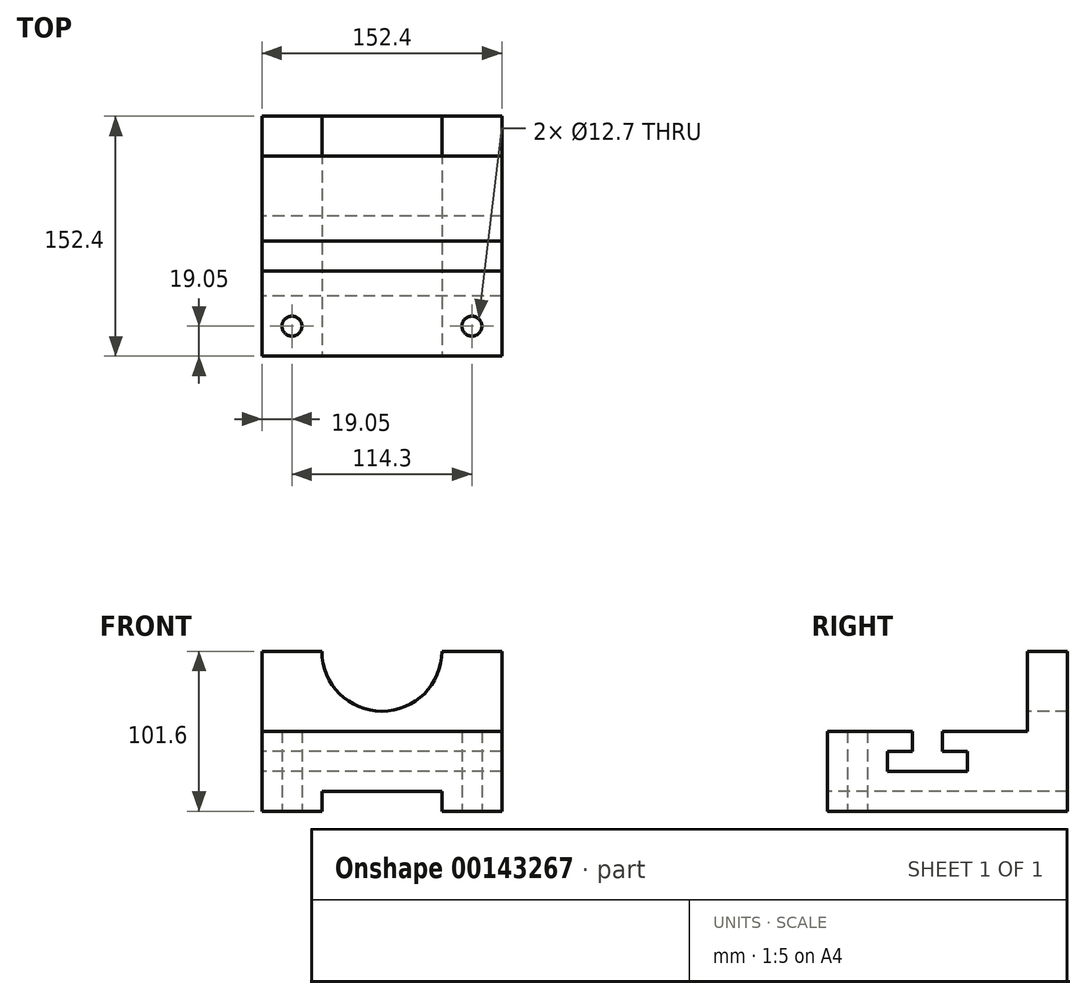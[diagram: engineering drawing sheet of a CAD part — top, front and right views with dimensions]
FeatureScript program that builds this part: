
annotation { "Feature Type Name" : "Feature", "Feature Type Description" : "" }
export const myFeature = defineFeature(function(context is Context, id is Id, definition is map)
    precondition{}
    {
        {
            var Q0;
            Q0=qCreatedBy(makeId("Right.planeOp"),FACE);
            var sketch = newSketch(context, id + "F0", { "sketchPlane" : qUnion([Q0])});
            skLineSegment(sketch, "E0", {"start": v(0, 0) * mm, "end": v(0, 50.8) * mm});
            skLineSegment(sketch, "E1", {"start": v(0, 50.8) * mm, "end": v(127, 50.8) * mm});
            skLineSegment(sketch, "E2", {"start": v(127, 50.8) * mm, "end": v(127, 101.6) * mm});
            skLineSegment(sketch, "E3", {"start": v(127, 101.6) * mm, "end": v(152.4, 101.6) * mm});
            skLineSegment(sketch, "E4", {"start": v(152.4, 101.6) * mm, "end": v(152.4, 0) * mm});
            skLineSegment(sketch, "E5", {"start": v(152.4, 0) * mm, "end": v(0, 0) * mm});
            skLineSegment(sketch, "E6", {"start": v(53.98, 50.8) * mm, "end": v(53.98, 38.1) * mm});
            skLineSegment(sketch, "E7", {"start": v(53.98, 38.1) * mm, "end": v(38.1, 38.1) * mm});
            skLineSegment(sketch, "E8", {"start": v(38.1, 38.1) * mm, "end": v(38.1, 25.4) * mm});
            skLineSegment(sketch, "E9", {"start": v(38.1, 25.4) * mm, "end": v(88.9, 25.4) * mm});
            skLineSegment(sketch, "E10", {"start": v(73.03, 50.8) * mm, "end": v(73.03, 38.1) * mm});
            skLineSegment(sketch, "E11", {"start": v(73.03, 38.1) * mm, "end": v(88.9, 38.1) * mm});
            skLineSegment(sketch, "E12", {"start": v(88.9, 38.1) * mm, "end": v(88.9, 25.4) * mm});
            skSolve(sketch);
        }
        {
            var Q0;
            {var subQ0=sQuery(id+"F0.wireOp",EDGE,"E0");Q0=makeQuery(id+"F0.imprint","IMPRINT",FACE,{"disambiguationData":[TD([[makeQuery(id+"F0.imprint","IMPRINT",EDGE,{"derivedFrom":subQ0}),-1.0]])]});}
            extrude(context, id + "F1", {"entities" : qUnion([Q0]), "depth" : 152.4 * mm});
        }
        {
            var Q0;
            Q0=qCreatedBy(makeId("Front.planeOp"),FACE);
            var sketch = newSketch(context, id + "F2", { "sketchPlane" : qUnion([Q0])});
            skLineSegment(sketch, "E13.0", {"start": v(152.4, 0) * mm, "end": v(0, 0) * mm});
            skLineSegment(sketch, "E14.0", {"start": v(152.4, 0) * mm, "end": v(152.4, 50.8) * mm});
            skLineSegment(sketch, "E15.0", {"start": v(0, 0) * mm, "end": v(0, 50.8) * mm});
            skLineSegment(sketch, "E16", {"start": v(38.1, 0) * mm, "end": v(38.1, 12.7) * mm});
            skLineSegment(sketch, "E17", {"start": v(38.1, 12.7) * mm, "end": v(114.3, 12.7) * mm});
            skLineSegment(sketch, "E18", {"start": v(114.3, 12.7) * mm, "end": v(114.3, 0) * mm});
            skSolve(sketch);
        }
        {
            var Q0;
            Q0 = qSketchRegion(id + "F2", true);
            extrude(context, id + "F3", {"entities" : qUnion([Q0]), "operationType" : NewBodyOperationType.REMOVE, "oppositeDirection" : true, "depth" : 152.4 * mm});
        }
        {
            var Q0;
            Q0=qCreatedBy(makeId("Front.planeOp"),FACE);
            var sketch = newSketch(context, id + "F4", { "sketchPlane" : qUnion([Q0])});
            skLineSegment(sketch, "E19.0", {"start": v(152.4, 101.6) * mm, "end": v(0, 101.6) * mm});
            skCircle(sketch, "E20", {"center": v(76.2, 101.6) * mm, "radius": 38.1 * mm});
            skSolve(sketch);
        }
        {
            var Q0;
            Q0 = qSketchRegion(id + "F4", true);
            extrude(context, id + "F5", {"entities" : qUnion([Q0]), "operationType" : NewBodyOperationType.REMOVE, "oppositeDirection" : true, "depth" : 171.7 * mm});
        }
        {
            var Q0;
            Q0=qCreatedBy(makeId("Top.planeOp"),FACE);
            var sketch = newSketch(context, id + "F6", { "sketchPlane" : qUnion([Q0])});
            skLineSegment(sketch, "E21.0", {"start": v(152.4, 0) * mm, "end": v(152.4, 53.98) * mm});
            skLineSegment(sketch, "E22.0", {"start": v(152.4, 0) * mm, "end": v(0, 0) * mm});
            skLineSegment(sketch, "E23.0.0", {"start": v(0, 53.98) * mm, "end": v(0, 0) * mm});
            skLineSegment(sketch, "E23.0.1", {"start": v(0, 0) * mm, "end": v(152.4, 0) * mm});
            skLineSegment(sketch, "E23.0.3", {"start": v(152.4, 53.98) * mm, "end": v(0, 53.98) * mm});
            skCircle(sketch, "E24", {"center": v(19.05, 19.05) * mm, "radius": 6.35 * mm});
            skCircle(sketch, "E25", {"center": v(133.35, 19.05) * mm, "radius": 6.35 * mm});
            skSolve(sketch);
        }
        {
            var Q0;
            Q0=qCreatedBy(makeId("Top.planeOp"),FACE);
            var sketch = newSketch(context, id + "F7", { "sketchPlane" : qUnion([Q0])});
            skCircle(sketch, "E26.0", {"center": v(19.05, 19.05) * mm, "radius": 6.35 * mm});
            skCircle(sketch, "E27.0", {"center": v(133.35, 19.05) * mm, "radius": 6.35 * mm});
            skSolve(sketch);
        }
        {
            var Q0;
            Q0 = qSketchRegion(id + "F7", true);
            extrude(context, id + "F8", {"entities" : qUnion([Q0]), "operationType" : NewBodyOperationType.REMOVE, "depth" : 152.4 * mm});
        }
    });
